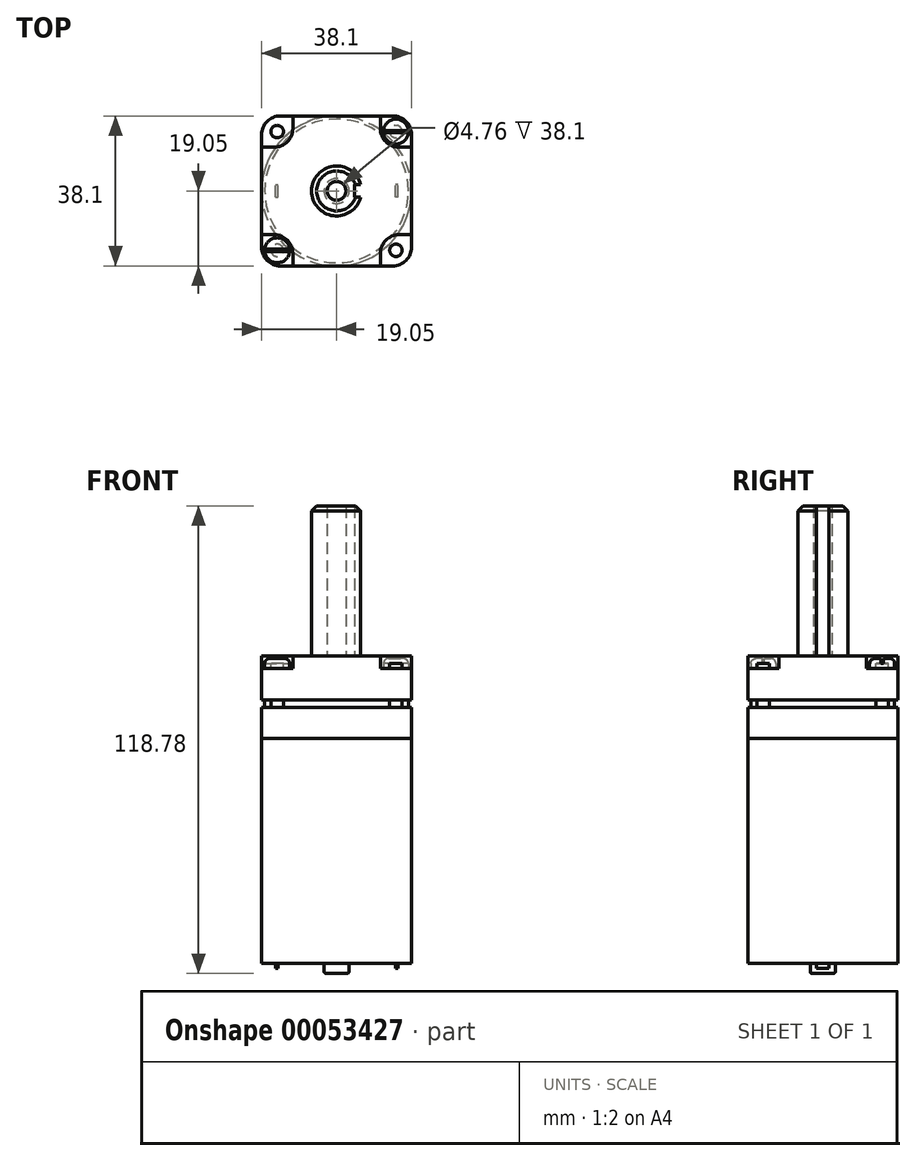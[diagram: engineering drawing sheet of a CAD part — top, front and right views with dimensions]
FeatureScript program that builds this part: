
annotation { "Feature Type Name" : "Feature", "Feature Type Description" : "" }
export const myFeature = defineFeature(function(context is Context, id is Id, definition is map)
    precondition{}
    {
        {
            var Q0;
            Q0=qCreatedBy(makeId("Top.planeOp"),FACE);
            var sketch = newSketch(context, id + "F0", { "sketchPlane" : qUnion([Q0])});
            skLineSegment(sketch, "E0.rect.bottom", {"start": v(-19.05, 19.05) * mm, "end": v(19.05, 19.05) * mm});
            skLineSegment(sketch, "E0.rect.top", {"start": v(-19.05, -19.05) * mm, "end": v(19.05, -19.05) * mm});
            skLineSegment(sketch, "E0.rect.left", {"start": v(-19.05, 19.05) * mm, "end": v(-19.05, -19.05) * mm});
            skLineSegment(sketch, "E0.rect.right", {"start": v(19.05, 19.05) * mm, "end": v(19.05, -19.05) * mm});
            skPoint(sketch, "E0.rect.middle", {"position": v(0, 0) * mm});
            skSolve(sketch);
        }
        {
            var Q0;
            Q0 = qSketchRegion(id + "F0", true);
            extrude(context, id + "F1", {"entities" : qUnion([Q0]), "depth" : 7.94 * mm});
        }
        {
            var Q0;
            Q0=makeQuery(id+"F1.opExtrude","CAP_FACE",FACE,{"disambiguationData":[OSD([sQuery(id+"F0.wireOp",EDGE,"E0.rect.bottom"),sQuery(id+"F0.wireOp",EDGE,"E0.rect.top"),sQuery(id+"F0.wireOp",EDGE,"E0.rect.left"),sQuery(id+"F0.wireOp",EDGE,"E0.rect.right")])],"isStart":false});
            var sketch = newSketch(context, id + "F2", { "sketchPlane" : qUnion([Q0])});
            skCircle(sketch, "E1", {"center": v(0, 0) * mm, "radius": 18.26 * mm});
            skSolve(sketch);
        }
        {
            var Q0;
            Q0=makeQuery(id+"F2.imprint","IMPRINT",FACE,{"disambiguationData":[TD([[makeQuery(id+"F2.imprint","IMPRINT",EDGE,{"derivedFrom":sQuery(id+"F2.wireOp",EDGE,"E1")}),1.0]])]});
            extrude(context, id + "F3", {"entities" : qUnion([Q0]), "operationType" : NewBodyOperationType.ADD, "depth" : (1 + (15 / 16)) * mm});
        }
        {
            var Q0;
            Q0=makeQuery(id+"F1.opExtrude","CAP_FACE",FACE,{"disambiguationData":[OSD([sQuery(id+"F0.wireOp",EDGE,"E0.rect.bottom"),sQuery(id+"F0.wireOp",EDGE,"E0.rect.top"),sQuery(id+"F0.wireOp",EDGE,"E0.rect.left"),sQuery(id+"F0.wireOp",EDGE,"E0.rect.right")])],"isStart":true});
            var sketch = newSketch(context, id + "F4", { "sketchPlane" : qUnion([Q0])});
            skCircle(sketch, "E2", {"center": v(0, 0) * mm, "radius": 19.05 * mm});
            skSolve(sketch);
        }
        {
            var Q0;
            {var subQ0=sQuery(id+"F4.wireOp",EDGE,"E2");var subQ1=makeQuery(id+"F4.imprint","INTERSECT",VERTEX,{"derivedFrom":[makeQuery(id+"F1.opExtrude","CAP_EDGE",EDGE,{"disambiguationData":[OSD([sQuery(id+"F0.wireOp",EDGE,"E0.rect.top")])],"isStart":true}),subQ0]});Q0=makeQuery(id+"F4.imprint","IMPRINT",FACE,{"disambiguationData":[TD([[makeQuery(id+"F4.imprint","IMPRINT",EDGE,{"disambiguationData":[TD([[subQ1,1.0]])],"derivedFrom":subQ0}),1.0]])]});}
            extrude(context, id + "F5", {"entities" : qUnion([Q0]), "operationType" : NewBodyOperationType.ADD, "depth" : 57.15 * mm});
        }
        {
            var Q0;
            Q0=makeQuery(id+"F3.opExtrude","CAP_FACE",FACE,{"disambiguationData":[OSD([sQuery(id+"F2.wireOp",EDGE,"E1")])],"isStart":false});
            var sketch = newSketch(context, id + "F6", { "sketchPlane" : qUnion([Q0])});
            skLineSegment(sketch, "E3.rect.bottom", {"start": v(19.05, -19.05) * mm, "end": v(-19.05, -19.05) * mm});
            skLineSegment(sketch, "E3.rect.top", {"start": v(19.05, 19.05) * mm, "end": v(-19.05, 19.05) * mm});
            skLineSegment(sketch, "E3.rect.left", {"start": v(19.05, -19.05) * mm, "end": v(19.05, 19.05) * mm});
            skLineSegment(sketch, "E3.rect.right", {"start": v(-19.05, -19.05) * mm, "end": v(-19.05, 19.05) * mm});
            skPoint(sketch, "E3.rect.middle", {"position": v(0, 0) * mm});
            skSolve(sketch);
        }
        {
            var Q0;
            Q0 = qSketchRegion(id + "F6", true);
            extrude(context, id + "F7", {"entities" : qUnion([Q0]), "operationType" : NewBodyOperationType.ADD, "depth" : 11.1 * mm});
        }
        {
            var Q0;
            Q0=makeQuery(id+"F7.opExtrude","CAP_FACE",FACE,{"disambiguationData":[OSD([sQuery(id+"F6.wireOp",EDGE,"E3.rect.bottom"),sQuery(id+"F6.wireOp",EDGE,"E3.rect.top"),sQuery(id+"F6.wireOp",EDGE,"E3.rect.left"),sQuery(id+"F6.wireOp",EDGE,"E3.rect.right")])],"isStart":false});
            var sketch = newSketch(context, id + "F8", { "sketchPlane" : qUnion([Q0])});
            skLineSegment(sketch, "E4", {"start": v(-19.05, -11.11) * mm, "end": v(-11.11, -11.11) * mm});
            skLineSegment(sketch, "E5", {"start": v(-11.11, -11.11) * mm, "end": v(-11.11, -19.05) * mm});
            skLineSegment(sketch, "E6", {"start": v(-11.11, -19.05) * mm, "end": v(-19.05, -19.05) * mm});
            skLineSegment(sketch, "E7", {"start": v(-19.05, -19.05) * mm, "end": v(-19.05, -11.11) * mm});
            skLineSegment(sketch, "E8.MirrorCS", {"start": v(11.11, -11.11) * mm, "end": v(11.11, -19.05) * mm});
            skLineSegment(sketch, "E9.MirrorCS", {"start": v(19.05, -11.11) * mm, "end": v(11.11, -11.11) * mm});
            skLineSegment(sketch, "E10.MirrorCS", {"start": v(19.05, -19.05) * mm, "end": v(19.05, -11.11) * mm});
            skLineSegment(sketch, "E11.MirrorCS", {"start": v(11.11, -19.05) * mm, "end": v(19.05, -19.05) * mm});
            skLineSegment(sketch, "E12.MirrorCS", {"start": v(19.05, 11.11) * mm, "end": v(11.11, 11.11) * mm});
            skLineSegment(sketch, "E13.MirrorCS", {"start": v(11.11, 11.11) * mm, "end": v(11.11, 19.05) * mm});
            skLineSegment(sketch, "E14.MirrorCS", {"start": v(11.11, 19.05) * mm, "end": v(19.05, 19.05) * mm});
            skLineSegment(sketch, "E15.MirrorCS", {"start": v(19.05, 19.05) * mm, "end": v(19.05, 11.11) * mm});
            skLineSegment(sketch, "E16.MirrorCS", {"start": v(-19.05, 11.11) * mm, "end": v(-11.11, 11.11) * mm});
            skLineSegment(sketch, "E17.MirrorCS", {"start": v(-11.11, 11.11) * mm, "end": v(-11.11, 19.05) * mm});
            skLineSegment(sketch, "E18.MirrorCS", {"start": v(-11.11, 19.05) * mm, "end": v(-19.05, 19.05) * mm});
            skLineSegment(sketch, "E19.MirrorCS", {"start": v(-19.05, 19.05) * mm, "end": v(-19.05, 11.11) * mm});
            skSolve(sketch);
        }
        {
            var Q0;
            Q0=makeQuery(id+"F8.imprint","IMPRINT",FACE,{"disambiguationData":[TD([[makeQuery(id+"F8.imprint","IMPRINT",EDGE,{"derivedFrom":sQuery(id+"F8.wireOp",EDGE,"E16.MirrorCS")}),1.0]])]});
            var Q1;
            Q1=makeQuery(id+"F8.imprint","IMPRINT",FACE,{"disambiguationData":[TD([[makeQuery(id+"F8.imprint","IMPRINT",EDGE,{"derivedFrom":sQuery(id+"F8.wireOp",EDGE,"E12.MirrorCS")}),-1.0]])]});
            var Q2;
            Q2=makeQuery(id+"F8.imprint","IMPRINT",FACE,{"disambiguationData":[TD([[makeQuery(id+"F8.imprint","IMPRINT",EDGE,{"derivedFrom":sQuery(id+"F8.wireOp",EDGE,"E8.MirrorCS")}),1.0]])]});
            var Q3;
            Q3=makeQuery(id+"F8.imprint","IMPRINT",FACE,{"disambiguationData":[TD([[makeQuery(id+"F8.imprint","IMPRINT",EDGE,{"derivedFrom":sQuery(id+"F8.wireOp",EDGE,"E4")}),-1.0]])]});
            extrude(context, id + "F9", {"entities" : qUnion([Q0, Q1, Q2, Q3]), "operationType" : NewBodyOperationType.REMOVE, "oppositeDirection" : true, "depth" : 3.17 * mm});
        }
        {
            var Q0;
            Q0=makeQuery(id+"F7.opExtrude","SWEPT_EDGE",EDGE,{"disambiguationData":[OSD([sQuery(id+"F6.wireOp",EDGE,"E3.rect.bottom"),sQuery(id+"F6.wireOp",EDGE,"E3.rect.right")])]});
            var Q1;
            Q1=makeQuery(id+"F7.opExtrude","SWEPT_EDGE",EDGE,{"disambiguationData":[OSD([sQuery(id+"F6.wireOp",EDGE,"E3.rect.bottom"),sQuery(id+"F6.wireOp",EDGE,"E3.rect.left")])]});
            var Q2;
            Q2=makeQuery(id+"F1.opExtrude","SWEPT_EDGE",EDGE,{"disambiguationData":[OSD([sQuery(id+"F0.wireOp",EDGE,"E0.rect.top"),sQuery(id+"F0.wireOp",EDGE,"E0.rect.right")])]});
            var Q3;
            Q3=makeQuery(id+"F1.opExtrude","SWEPT_EDGE",EDGE,{"disambiguationData":[OSD([sQuery(id+"F0.wireOp",EDGE,"E0.rect.top"),sQuery(id+"F0.wireOp",EDGE,"E0.rect.left")])]});
            var Q4;
            Q4=makeQuery(id+"F1.opExtrude","SWEPT_EDGE",EDGE,{"disambiguationData":[OSD([sQuery(id+"F0.wireOp",EDGE,"E0.rect.bottom"),sQuery(id+"F0.wireOp",EDGE,"E0.rect.right")])]});
            var Q5;
            Q5=makeQuery(id+"F7.opExtrude","SWEPT_EDGE",EDGE,{"disambiguationData":[OSD([sQuery(id+"F6.wireOp",EDGE,"E3.rect.top"),sQuery(id+"F6.wireOp",EDGE,"E3.rect.left")])]});
            var Q6;
            Q6=makeQuery(id+"F1.opExtrude","SWEPT_EDGE",EDGE,{"disambiguationData":[OSD([sQuery(id+"F0.wireOp",EDGE,"E0.rect.bottom"),sQuery(id+"F0.wireOp",EDGE,"E0.rect.left")])]});
            var Q7;
            Q7=makeQuery(id+"F7.opExtrude","SWEPT_EDGE",EDGE,{"disambiguationData":[OSD([sQuery(id+"F6.wireOp",EDGE,"E3.rect.top"),sQuery(id+"F6.wireOp",EDGE,"E3.rect.right")])]});
            fillet(context, id + "F10", {"entities" : qUnion([Q0, Q1, Q2, Q3, Q4, Q5, Q6, Q7]), "radius" : 4.76 * mm, "tangentPropagation" : true, "allowEdgeOverflow" : false});
        }
        {
            var Q0;
            Q0=makeQuery(id+"F9.boolean.opBoolean","COPY",EDGE,{"derivedFrom":makeQuery(id+"F9.opExtrude","SWEPT_EDGE",EDGE,{"disambiguationData":[OSD([sQuery(id+"F8.wireOp",EDGE,"E8.MirrorCS"),sQuery(id+"F8.wireOp",EDGE,"E9.MirrorCS")])]})});
            var Q1;
            Q1=makeQuery(id+"F9.boolean.opBoolean","COPY",EDGE,{"derivedFrom":makeQuery(id+"F9.opExtrude","SWEPT_EDGE",EDGE,{"disambiguationData":[OSD([sQuery(id+"F8.wireOp",EDGE,"E4"),sQuery(id+"F8.wireOp",EDGE,"E5")])]})});
            var Q2;
            Q2=makeQuery(id+"F9.boolean.opBoolean","COPY",EDGE,{"derivedFrom":makeQuery(id+"F9.opExtrude","SWEPT_EDGE",EDGE,{"disambiguationData":[OSD([sQuery(id+"F8.wireOp",EDGE,"E12.MirrorCS"),sQuery(id+"F8.wireOp",EDGE,"E13.MirrorCS")])]})});
            var Q3;
            Q3=makeQuery(id+"F9.boolean.opBoolean","COPY",EDGE,{"derivedFrom":makeQuery(id+"F9.opExtrude","SWEPT_EDGE",EDGE,{"disambiguationData":[OSD([sQuery(id+"F8.wireOp",EDGE,"E16.MirrorCS"),sQuery(id+"F8.wireOp",EDGE,"E17.MirrorCS")])]})});
            fillet(context, id + "F11", {"entities" : qUnion([Q0, Q1, Q2, Q3]), "radius" : 4.76 * mm, "tangentPropagation" : true, "allowEdgeOverflow" : false});
        }
        {
            var Q0;
            Q0=makeQuery(id+"F9.boolean.opBoolean","COPY",FACE,{"derivedFrom":makeQuery(id+"F9.opExtrude","CAP_FACE",FACE,{"disambiguationData":[OSD([sQuery(id+"F8.wireOp",EDGE,"E12.MirrorCS"),sQuery(id+"F8.wireOp",EDGE,"E13.MirrorCS"),sQuery(id+"F8.wireOp",EDGE,"E14.MirrorCS"),sQuery(id+"F8.wireOp",EDGE,"E15.MirrorCS")])],"isStart":false})});
            var sketch = newSketch(context, id + "F12", { "sketchPlane" : qUnion([Q0])});
            skCircle(sketch, "E20", {"center": v(15.08, 15.08) * mm, "radius": 3.18 * mm});
            skCircle(sketch, "E21.MirrorC", {"center": v(-15.08, 15.08) * mm, "radius": 3.18 * mm});
            skCircle(sketch, "E22.MirrorC", {"center": v(-15.08, -15.08) * mm, "radius": 3.18 * mm});
            skCircle(sketch, "E23.MirrorC", {"center": v(15.08, -15.08) * mm, "radius": 3.18 * mm});
            skSolve(sketch);
        }
        {
            var Q0;
            Q0=makeQuery(id+"F12.imprint","IMPRINT",FACE,{"disambiguationData":[TD([[makeQuery(id+"F12.imprint","IMPRINT",EDGE,{"derivedFrom":sQuery(id+"F12.wireOp",EDGE,"E20")}),1.0]])]});
            var Q1;
            Q1=makeQuery(id+"F12.imprint","IMPRINT",FACE,{"disambiguationData":[TD([[makeQuery(id+"F12.imprint","IMPRINT",EDGE,{"derivedFrom":sQuery(id+"F12.wireOp",EDGE,"E21.MirrorC")}),-1.0]])]});
            var Q2;
            Q2=makeQuery(id+"F12.imprint","IMPRINT",FACE,{"disambiguationData":[TD([[makeQuery(id+"F12.imprint","IMPRINT",EDGE,{"derivedFrom":sQuery(id+"F12.wireOp",EDGE,"E22.MirrorC")}),1.0]])]});
            var Q3;
            Q3=makeQuery(id+"F12.imprint","IMPRINT",FACE,{"disambiguationData":[TD([[makeQuery(id+"F12.imprint","IMPRINT",EDGE,{"derivedFrom":sQuery(id+"F12.wireOp",EDGE,"E23.MirrorC")}),-1.0]])]});
            extrude(context, id + "F13", {"entities" : qUnion([Q0, Q1, Q2, Q3]), "operationType" : NewBodyOperationType.ADD, "depth" : 2.54 * mm});
        }
        {
            var Q0;
            Q0=makeQuery(id+"F13.opExtrude","CAP_EDGE",EDGE,{"disambiguationData":[OSD([sQuery(id+"F12.wireOp",EDGE,"E21.MirrorC")])],"isStart":false});
            var Q1;
            Q1=makeQuery(id+"F13.opExtrude","CAP_EDGE",EDGE,{"disambiguationData":[OSD([sQuery(id+"F12.wireOp",EDGE,"E20")])],"isStart":false});
            var Q2;
            Q2=makeQuery(id+"F13.opExtrude","CAP_EDGE",EDGE,{"disambiguationData":[OSD([sQuery(id+"F12.wireOp",EDGE,"E23.MirrorC")])],"isStart":false});
            var Q3;
            Q3=makeQuery(id+"F13.opExtrude","CAP_EDGE",EDGE,{"disambiguationData":[OSD([sQuery(id+"F12.wireOp",EDGE,"E22.MirrorC")])],"isStart":false});
            fillet(context, id + "F14", {"entities" : qUnion([Q0, Q1, Q2, Q3]), "radius" : 1.27 * mm, "tangentPropagation" : true, "allowEdgeOverflow" : false});
        }
        {
            var Q0;
            Q0=makeQuery(id+"F13.opExtrude","CAP_FACE",FACE,{"disambiguationData":[OSD([sQuery(id+"F12.wireOp",EDGE,"E20")])],"isStart":false});
            var sketch = newSketch(context, id + "F15", { "sketchPlane" : qUnion([Q0])});
            skLineSegment(sketch, "E24.rect.bottom", {"start": v(18.39, 15.34) * mm, "end": v(11.78, 15.34) * mm});
            skLineSegment(sketch, "E24.rect.top", {"start": v(18.39, 14.82) * mm, "end": v(11.78, 14.82) * mm});
            skLineSegment(sketch, "E24.rect.left", {"start": v(18.39, 15.34) * mm, "end": v(18.39, 14.82) * mm});
            skLineSegment(sketch, "E24.rect.right", {"start": v(11.78, 15.34) * mm, "end": v(11.78, 14.82) * mm});
            skPoint(sketch, "E24.rect.middle", {"position": v(15.08, 15.08) * mm});
            skLineSegment(sketch, "E25.MirrorCS", {"start": v(-18.39, 15.34) * mm, "end": v(-11.78, 15.34) * mm});
            skLineSegment(sketch, "E26.MirrorCS", {"start": v(-18.39, 14.82) * mm, "end": v(-11.78, 14.82) * mm});
            skLineSegment(sketch, "E27.MirrorCS", {"start": v(-11.78, 15.34) * mm, "end": v(-11.78, 14.82) * mm});
            skLineSegment(sketch, "E28.MirrorCS", {"start": v(-18.39, 15.34) * mm, "end": v(-18.39, 14.82) * mm});
            skLineSegment(sketch, "E29.MirrorCS", {"start": v(18.39, -15.34) * mm, "end": v(11.78, -15.34) * mm});
            skLineSegment(sketch, "E30.MirrorCS", {"start": v(18.39, -14.82) * mm, "end": v(11.78, -14.82) * mm});
            skLineSegment(sketch, "E31.MirrorCS", {"start": v(11.78, -15.34) * mm, "end": v(11.78, -14.82) * mm});
            skLineSegment(sketch, "E32.MirrorCS", {"start": v(18.39, -15.34) * mm, "end": v(18.39, -14.82) * mm});
            skLineSegment(sketch, "E33.MirrorCS", {"start": v(-18.39, -14.82) * mm, "end": v(-11.78, -14.82) * mm});
            skLineSegment(sketch, "E34.MirrorCS", {"start": v(-18.39, -15.34) * mm, "end": v(-11.78, -15.34) * mm});
            skLineSegment(sketch, "E35.MirrorCS", {"start": v(-11.78, -15.34) * mm, "end": v(-11.78, -14.82) * mm});
            skLineSegment(sketch, "E36.MirrorCS", {"start": v(-18.39, -15.34) * mm, "end": v(-18.39, -14.82) * mm});
            skSolve(sketch);
        }
        {
            var Q0;
            Q0 = qSketchRegion(id + "F15", true);
            extrude(context, id + "F16", {"entities" : qUnion([Q0]), "operationType" : NewBodyOperationType.REMOVE, "oppositeDirection" : true, "depth" : 1.27 * mm});
        }
        {
            var Q0;
            Q0=makeQuery(id+"F16.boolean.opBoolean","COPY",FACE,{"derivedFrom":makeQuery(id+"F16.opExtrude","CAP_FACE",FACE,{"disambiguationData":[OSD([sQuery(id+"F15.wireOp",EDGE,"E24.rect.bottom"),sQuery(id+"F15.wireOp",EDGE,"E24.rect.top"),sQuery(id+"F15.wireOp",EDGE,"E24.rect.left"),sQuery(id+"F15.wireOp",EDGE,"E24.rect.right")])],"isStart":false})});
            var sketch = newSketch(context, id + "F17", { "sketchPlane" : qUnion([Q0])});
            skCircle(sketch, "E37", {"center": v(15.08, 15.08) * mm, "radius": 1.59 * mm});
            skCircle(sketch, "E38.MirrorC", {"center": v(-15.08, 15.08) * mm, "radius": 1.59 * mm});
            skCircle(sketch, "E39.MirrorC", {"center": v(-15.08, -15.08) * mm, "radius": 1.59 * mm});
            skCircle(sketch, "E40.MirrorC", {"center": v(15.08, -15.08) * mm, "radius": 1.59 * mm});
            skSolve(sketch);
        }
        {
            var Q0;
            Q0 = qSketchRegion(id + "F17", true);
            var Q1;
            Q1=makeQuery(id+"F1.opExtrude","CAP_FACE",FACE,{"disambiguationData":[OSD([sQuery(id+"F0.wireOp",EDGE,"E0.rect.bottom"),sQuery(id+"F0.wireOp",EDGE,"E0.rect.top"),sQuery(id+"F0.wireOp",EDGE,"E0.rect.left"),sQuery(id+"F0.wireOp",EDGE,"E0.rect.right")])],"isStart":false});
            extrude(context, id + "F18", {"entities" : qUnion([Q0]), "operationType" : NewBodyOperationType.ADD, "endBound" : BoundingType.UP_TO_SURFACE, "oppositeDirection" : true, "endBoundEntityFace" : qUnion([Q1]), "depth" : 25.4 * mm});
        }
        {
            var Q0;
            Q0=makeQuery(id+"F5.opExtrude","CAP_FACE",FACE,{"disambiguationData":[OSD([sQuery(id+"F4.wireOp",EDGE,"E2")])],"isStart":false});
            var sketch = newSketch(context, id + "F19", { "sketchPlane" : qUnion([Q0])});
            skCircle(sketch, "E41", {"center": v(0, 0) * mm, "radius": 3.18 * mm});
            skLineSegment(sketch, "E42.rect.bottom", {"start": v(15.56, 1.59) * mm, "end": v(14.92, 1.59) * mm});
            skLineSegment(sketch, "E42.rect.top", {"start": v(15.56, -1.59) * mm, "end": v(14.92, -1.59) * mm});
            skLineSegment(sketch, "E42.rect.left", {"start": v(15.56, 1.59) * mm, "end": v(15.56, -1.59) * mm});
            skLineSegment(sketch, "E42.rect.right", {"start": v(14.92, 1.59) * mm, "end": v(14.92, -1.59) * mm});
            skPoint(sketch, "E42.rect.middle", {"position": v(15.24, 0) * mm});
            skLineSegment(sketch, "E43.MirrorCS", {"start": v(-15.56, -1.59) * mm, "end": v(-14.92, -1.59) * mm});
            skLineSegment(sketch, "E44.MirrorCS", {"start": v(-15.56, 1.59) * mm, "end": v(-14.92, 1.59) * mm});
            skPoint(sketch, "E45.MirrorP", {"position": v(-15.24, 0) * mm});
            skLineSegment(sketch, "E46.MirrorCS", {"start": v(-14.92, 1.59) * mm, "end": v(-14.92, -1.59) * mm});
            skLineSegment(sketch, "E47.MirrorCS", {"start": v(-15.56, 1.59) * mm, "end": v(-15.56, -1.59) * mm});
            skSolve(sketch);
        }
        {
            var Q0;
            Q0=makeQuery(id+"F19.imprint","IMPRINT",FACE,{"disambiguationData":[TD([[makeQuery(id+"F19.imprint","IMPRINT",EDGE,{"derivedFrom":sQuery(id+"F19.wireOp",EDGE,"E41")}),1.0]])]});
            extrude(context, id + "F20", {"entities" : qUnion([Q0]), "operationType" : NewBodyOperationType.ADD, "depth" : 2.54 * mm});
        }
        {
            var Q0;
            Q0=makeQuery(id+"F7.opExtrude","CAP_FACE",FACE,{"disambiguationData":[OSD([sQuery(id+"F6.wireOp",EDGE,"E3.rect.bottom"),sQuery(id+"F6.wireOp",EDGE,"E3.rect.top"),sQuery(id+"F6.wireOp",EDGE,"E3.rect.left"),sQuery(id+"F6.wireOp",EDGE,"E3.rect.right")])],"isStart":false});
            var sketch = newSketch(context, id + "F21", { "sketchPlane" : qUnion([Q0])});
            skCircle(sketch, "E48", {"center": v(0, 0) * mm, "radius": 2.38 * mm});
            skLineSegment(sketch, "E49", {"start": v(4.56, 0) * mm, "end": v(4.56, -1.59) * mm});
            skLineSegment(sketch, "E50", {"start": v(4.56, -1.59) * mm, "end": v(6.15, -1.59) * mm});
            skLineSegment(sketch, "E51", {"start": v(4.56, 0) * mm, "end": v(4.56, 1.59) * mm});
            skLineSegment(sketch, "E52", {"start": v(4.56, 1.59) * mm, "end": v(6.15, 1.59) * mm});
            skArc(sketch, "E53", {"start": v(6.15, 1.59) * mm, "mid": v(-6.35, 0) * mm, "end": v(6.15, -1.59) * mm});
            skSolve(sketch);
        }
        {
            var Q0;
            Q0 = qSketchRegion(id + "F19", true);
            extrude(context, id + "F22", {"entities" : qUnion([Q0]), "operationType" : NewBodyOperationType.ADD, "depth" : 1.27 * mm});
        }
        {
            var Q0;
            Q0=makeQuery(id+"F20.opExtrude","SWEPT_FACE",FACE,{"disambiguationData":[OSD([sQuery(id+"F19.wireOp",EDGE,"E41")])]});
            fillet(context, id + "F23", {"entities" : qUnion([Q0]), "radius" : 0.5 * mm, "tangentPropagation" : true, "allowEdgeOverflow" : false});
        }
        {
            var Q0;
            Q0 = qSketchRegion(id + "F21", true);
            extrude(context, id + "F24", {"entities" : qUnion([Q0]), "operationType" : NewBodyOperationType.ADD, "depth" : 38.1 * mm});
        }
        {
            var Q0;
            Q0=makeQuery(id+"F24.opExtrude","CAP_EDGE",EDGE,{"disambiguationData":[OSD([sQuery(id+"F21.wireOp",EDGE,"E53")])],"isStart":false});
            chamfer(context, id + "F25", {"entities" : qUnion([Q0]), "width" : 1.27 * mm, "tangentPropagation" : true});
        }
    });
